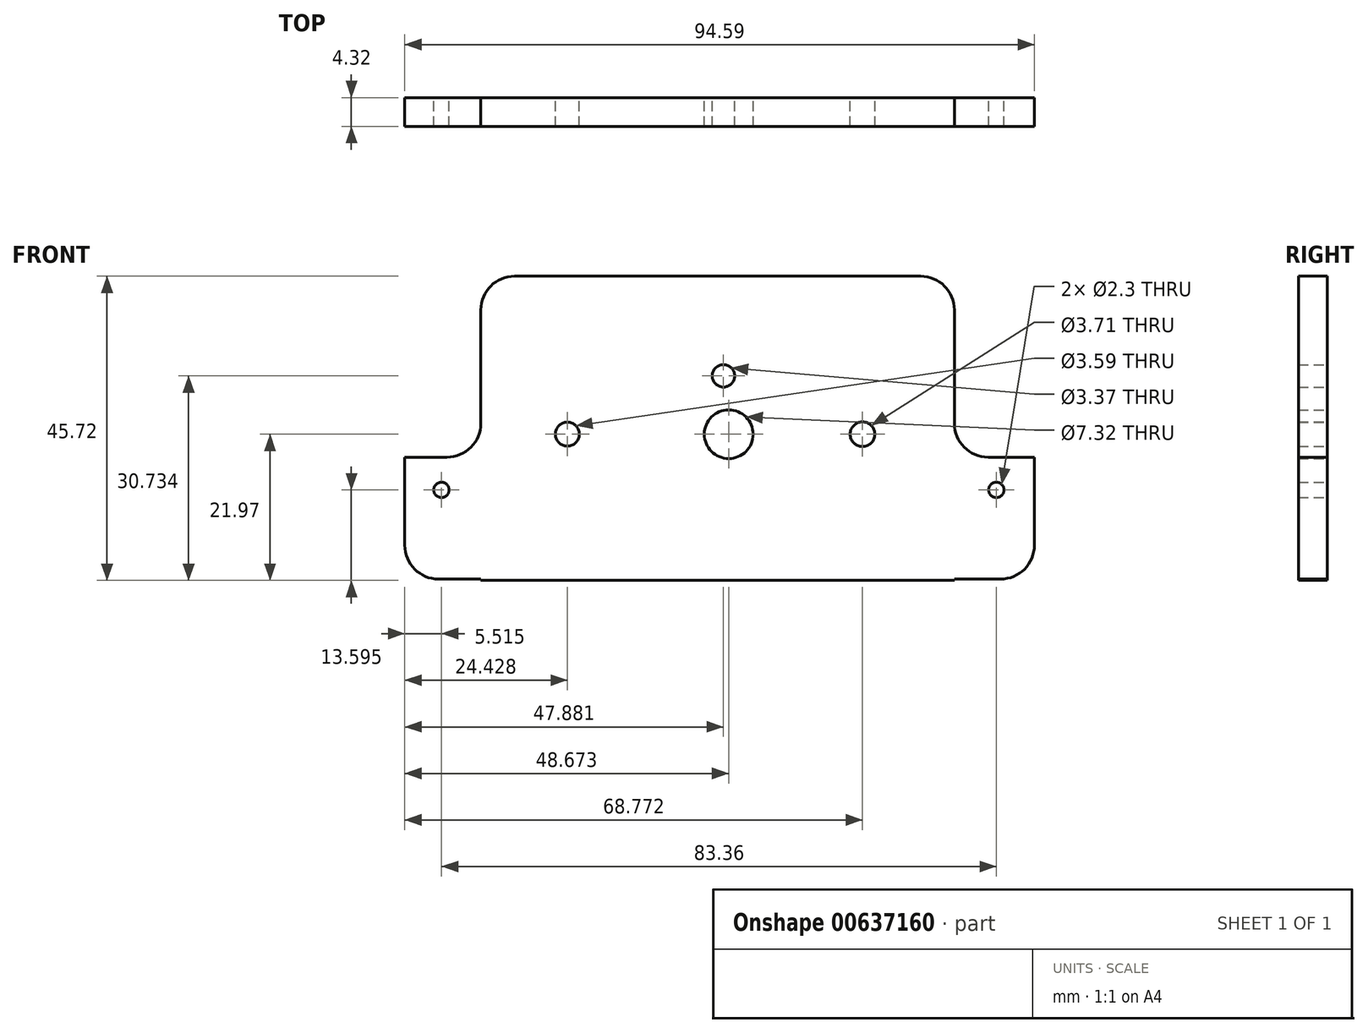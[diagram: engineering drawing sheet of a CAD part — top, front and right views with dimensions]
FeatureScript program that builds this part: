
annotation { "Feature Type Name" : "Feature", "Feature Type Description" : "" }
export const myFeature = defineFeature(function(context is Context, id is Id, definition is map)
    precondition{}
    {
        {
            var Q0;
            Q0=qCreatedBy(makeId("Front.planeOp"),FACE);
            var sketch = newSketch(context, id + "F0", { "sketchPlane" : qUnion([Q0])});
            skLineSegment(sketch, "E0.bottom", {"start": v(-30.05, 23.75) * mm, "end": v(41.09, 23.75) * mm});
            skLineSegment(sketch, "E0.top", {"start": v(-30.05, -21.97) * mm, "end": v(41.09, -21.97) * mm});
            skLineSegment(sketch, "E0.left", {"start": v(-30.05, 23.75) * mm, "end": v(-30.05, -21.97) * mm});
            skLineSegment(sketch, "E0.right", {"start": v(41.09, 23.75) * mm, "end": v(41.09, -21.97) * mm});
            skLineSegment(sketch, "E1.bottom", {"start": v(-30.05, -3.45) * mm, "end": v(-41.48, -3.45) * mm});
            skLineSegment(sketch, "E1.top", {"start": v(-30.05, -21.78) * mm, "end": v(-41.48, -21.78) * mm});
            skLineSegment(sketch, "E1.left", {"start": v(-30.05, -3.45) * mm, "end": v(-30.05, -21.78) * mm});
            skLineSegment(sketch, "E1.right", {"start": v(-41.48, -3.45) * mm, "end": v(-41.48, -21.78) * mm});
            skPoint(sketch, "E2.oppositeSnap0", {"position": v(-35.77, -21.78) * mm});
            skLineSegment(sketch, "E2.bottom", {"start": v(41.09, -3.45) * mm, "end": v(53.11, -3.45) * mm});
            skLineSegment(sketch, "E2.top", {"start": v(41.09, -21.78) * mm, "end": v(53.11, -21.78) * mm});
            skLineSegment(sketch, "E2.left", {"start": v(41.09, -3.45) * mm, "end": v(41.09, -21.78) * mm});
            skLineSegment(sketch, "E2.right", {"start": v(53.11, -3.45) * mm, "end": v(53.11, -21.78) * mm});
            skCircle(sketch, "E3", {"center": v(7.2, 0) * mm, "radius": 3.66 * mm});
            skCircle(sketch, "E4", {"center": v(-35.97, -8.38) * mm, "radius": 1.15 * mm});
            skCircle(sketch, "E5", {"center": v(47.4, -8.38) * mm, "radius": 1.15 * mm});
            skCircle(sketch, "E6", {"center": v(6.4, 8.76) * mm, "radius": 1.68 * mm});
            skCircle(sketch, "E7", {"center": v(-17.05, 0) * mm, "radius": 1.8 * mm});
            skCircle(sketch, "E8", {"center": v(27.3, 0) * mm, "radius": 1.85 * mm});
            skSolve(sketch);
        }
        {
            var Q0;
            {var subQ4=sQuery(id+"F0.wireOp",EDGE,"E0.bottom");Q0=makeQuery(id+"F0.imprint","IMPRINT",FACE,{"disambiguationData":[TD([[makeQuery(id+"F0.imprint","IMPRINT",EDGE,{"derivedFrom":subQ4}),-1.0]])]});}
            var Q1;
            Q1=makeQuery(id+"F0.imprint","IMPRINT",FACE,{"disambiguationData":[TD([[makeQuery(id+"F0.imprint","IMPRINT",EDGE,{"derivedFrom":sQuery(id+"F0.wireOp",EDGE,"E1.bottom")}),1.0]])]});
            var Q2;
            Q2=makeQuery(id+"F0.imprint","IMPRINT",FACE,{"disambiguationData":[TD([[makeQuery(id+"F0.imprint","IMPRINT",EDGE,{"derivedFrom":sQuery(id+"F0.wireOp",EDGE,"E2.bottom")}),-1.0]])]});
            extrude(context, id + "F1", {"entities" : qUnion([Q0, Q1, Q2]), "depth" : 4.32 * mm, "offsetDistance" : 25.4 * mm});
        }
        {
            var Q0;
            Q0=makeQuery(id+"F1.opExtrude","SWEPT_EDGE",EDGE,{"disambiguationData":[OSD([sQuery(id+"F0.wireOp",EDGE,"E0.bottom"),sQuery(id+"F0.wireOp",EDGE,"E0.left")])]});
            var Q1;
            Q1=makeQuery(id+"F1.opExtrude","SWEPT_EDGE",EDGE,{"disambiguationData":[OSD([sQuery(id+"F0.wireOp",EDGE,"E0.bottom"),sQuery(id+"F0.wireOp",EDGE,"E0.right")])]});
            var Q2;
            Q2=makeQuery(id+"F1.opExtrude","SWEPT_EDGE",EDGE,{"disambiguationData":[OSD([sQuery(id+"F0.wireOp",EDGE,"E0.left"),sQuery(id+"F0.wireOp",EDGE,"E1.bottom"),sQuery(id+"F0.wireOp",EDGE,"E1.left")])]});
            var Q3;
            Q3=makeQuery(id+"F1.opExtrude","SWEPT_EDGE",EDGE,{"disambiguationData":[OSD([sQuery(id+"F0.wireOp",EDGE,"E0.right"),sQuery(id+"F0.wireOp",EDGE,"E2.bottom"),sQuery(id+"F0.wireOp",EDGE,"E2.left")])]});
            var Q4;
            Q4=makeQuery(id+"F1.opExtrude","SWEPT_EDGE",EDGE,{"disambiguationData":[OSD([sQuery(id+"F0.wireOp",EDGE,"E2.top"),sQuery(id+"F0.wireOp",EDGE,"E2.right")])]});
            var Q5;
            Q5=makeQuery(id+"F1.opExtrude","SWEPT_EDGE",EDGE,{"disambiguationData":[OSD([sQuery(id+"F0.wireOp",EDGE,"E1.top"),sQuery(id+"F0.wireOp",EDGE,"E1.right")])]});
            fillet(context, id + "F2", {"entities" : qUnion([Q0, Q1, Q2, Q3, Q4, Q5]), "radius" : 5.08 * mm, "tangentPropagation" : true, "allowEdgeOverflow" : false});
        }
    });
